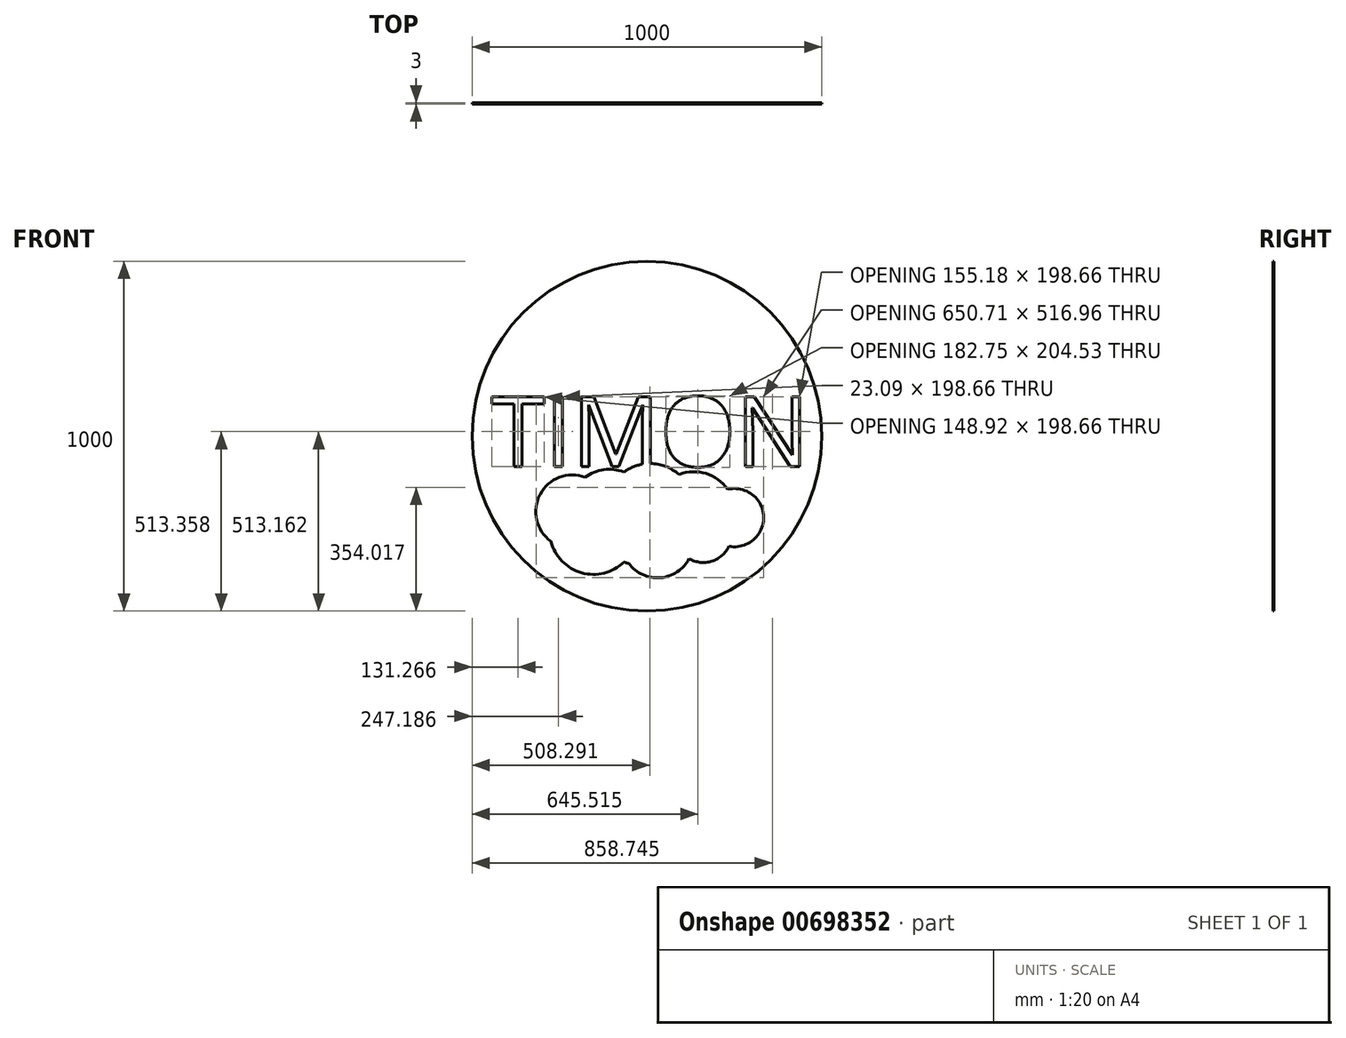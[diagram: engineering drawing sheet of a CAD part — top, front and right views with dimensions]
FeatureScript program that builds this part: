
annotation { "Feature Type Name" : "Feature", "Feature Type Description" : "" }
export const myFeature = defineFeature(function(context is Context, id is Id, definition is map)
    precondition{}
    {
        {
            var Q0;
            Q0=qCreatedBy(makeId("Front.planeOp"),FACE);
            var sketch = newSketch(context, id + "F0", { "sketchPlane" : qUnion([Q0])});
            skCircle(sketch, "E0", {"center": v(0, 0) * mm, "radius": 500 * mm});
            skText(sketch, "E1", { "text": "TIMON \n", "fontName": "OpenSans-Regular.ttf"});
            skCircle(sketch, "E2", {"center": v(-212.9, -215.57) * mm, "radius": 105.06 * mm});
            skCircle(sketch, "E3", {"center": v(-107.93, -211.2) * mm, "radius": 116.6 * mm});
            skCircle(sketch, "E4", {"center": v(8.5, -205.19) * mm, "radius": 127 * mm});
            skCircle(sketch, "E5", {"center": v(134.87, -217.8) * mm, "radius": 116.46 * mm});
            skCircle(sketch, "E6", {"center": v(250.37, -232.76) * mm, "radius": 83.3 * mm});
            skCircle(sketch, "E7", {"center": v(161.62, -280.22) * mm, "radius": 80.78 * mm});
            skCircle(sketch, "E8", {"center": v(-30.1, -266.84) * mm, "radius": 99.42 * mm});
            skCircle(sketch, "E9", {"center": v(30.1, -302.51) * mm, "radius": 102.28 * mm});
            skCircle(sketch, "E10", {"center": v(-152.71, -269.07) * mm, "radius": 125.87 * mm});
            const initialGuessF0  = {"E1": [-0.44563, -0.08617, 1, 0, 0.20036]};
            skSetInitialGuess(sketch, initialGuessF0);
            skSolve(sketch);
        }
        {
            var Q0;
            Q0=makeQuery(id+"F0.imprint","IMPRINT",FACE,{"disambiguationData":[TD([[makeQuery(id+"F0.imprint","IMPRINT",EDGE,{"derivedFrom":sQuery(id+"F0.wireOp",EDGE,"E0")}),1.0]])]});
            extrude(context, id + "F1", {"entities" : qUnion([Q0]), "depth" : 3 * mm, "offsetDistance" : 25 * mm});
        }
    });
